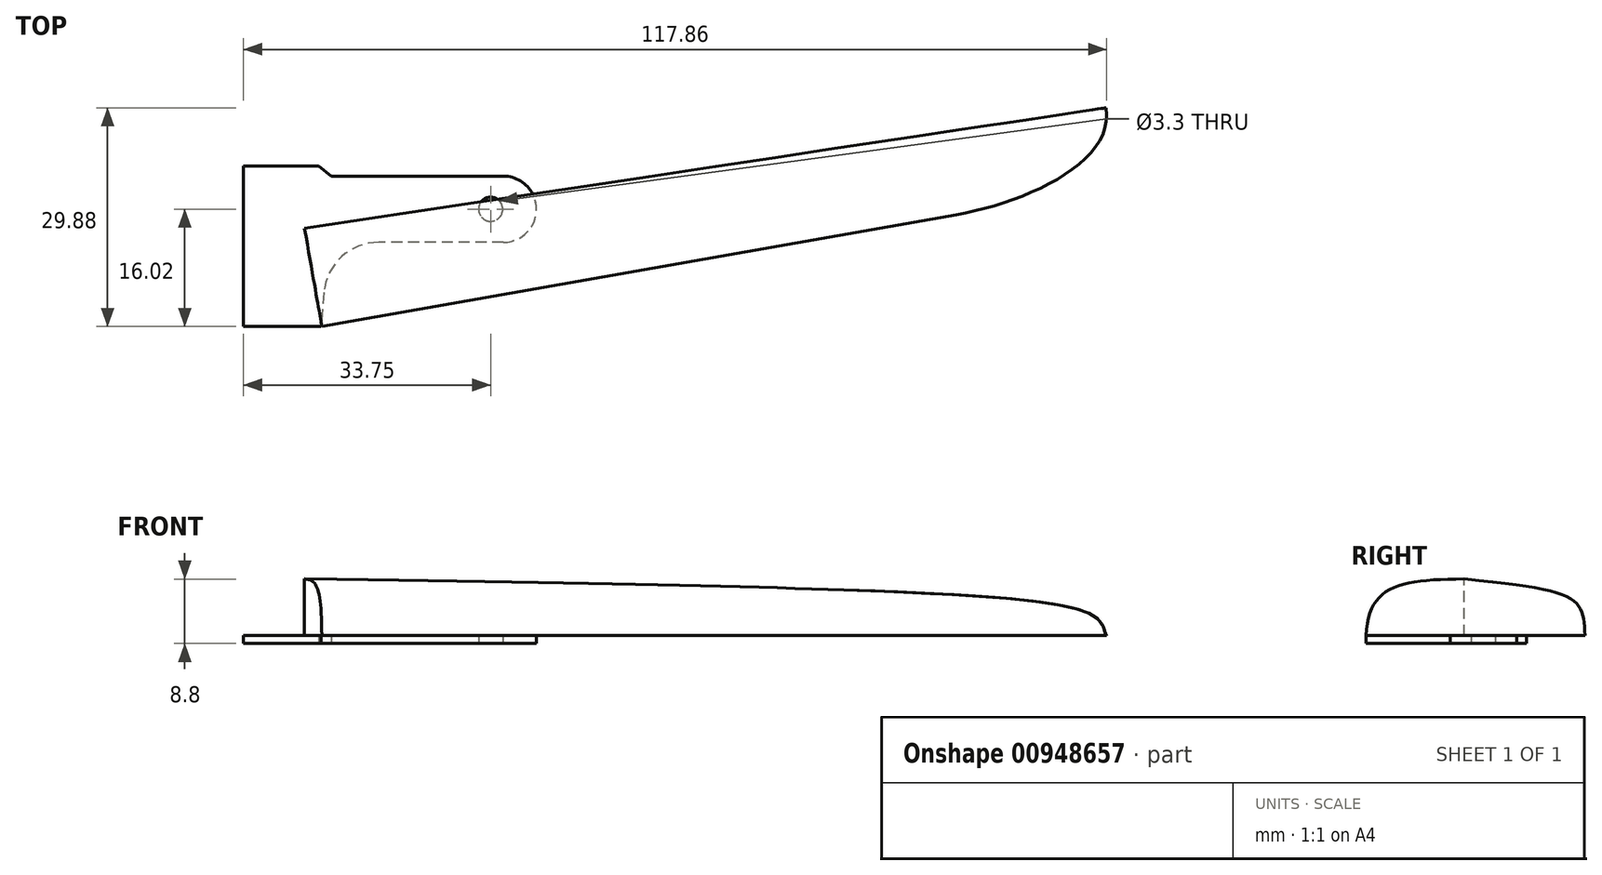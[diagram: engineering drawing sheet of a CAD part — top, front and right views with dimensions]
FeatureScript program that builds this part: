
annotation { "Feature Type Name" : "Feature", "Feature Type Description" : "" }
export const myFeature = defineFeature(function(context is Context, id is Id, definition is map)
    precondition{}
    {
        {
            var Q0;
            Q0=qCreatedBy(makeId("Top.planeOp"),FACE);
            var sketch = newSketch(context, id + "F0", { "sketchPlane" : qUnion([Q0]), "disableImprinting" : false});
            skCircle(sketch, "E0", {"center": v(0, 0) * mm, "radius": 1.65 * mm});
            skLineSegment(sketch, "E1", {"start": v(1.73, 4.52) * mm, "end": v(-21.75, 4.52) * mm});
            skArc(sketch, "E2", {"start": v(1.73, 4.52) * mm, "mid": v(6.25, 0) * mm, "end": v(1.73, -4.52) * mm});
            skLineSegment(sketch, "E3", {"start": v(1.73, -4.52) * mm, "end": v(-15.28, -4.52) * mm});
            skLineSegment(sketch, "E4", {"start": v(6.25, 0) * mm, "end": v(1.65, 0) * mm, "construction": true});
            skLineSegment(sketch, "E5", {"start": v(-21.75, 4.52) * mm, "end": v(-23.45, 5.9) * mm});
            skLineSegment(sketch, "E6", {"start": v(-23.45, 5.9) * mm, "end": v(-33.75, 5.9) * mm});
            skArc(sketch, "E7", {"start": v(-15.28, -4.52) * mm, "mid": v(-20.35, -6.5) * mm, "end": v(-22.75, -11.38) * mm});
            skLineSegment(sketch, "E8", {"start": v(-22.75, -11.38) * mm, "end": v(-23.15, -16.02) * mm});
            skLineSegment(sketch, "E9", {"start": v(-23.15, -16.02) * mm, "end": v(-33.75, -16.02) * mm});
            skLineSegment(sketch, "E10", {"start": v(-33.75, -16.02) * mm, "end": v(-33.75, 5.9) * mm});
            skSolve(sketch);
        }
        {
            var Q0;
            Q0 = qSketchRegion(id + "F0", true);
            extrude(context, id + "F1", {"entities" : qUnion([Q0]), "flatOperationType" : FlatOperationType.REMOVE, "thickness1" : 5 * mm, "thickness2" : 0 * mm, "thickness" : 5 * mm, "depth" : 1.06 * mm, "offsetDistance" : 25 * mm, "startOffsetBound" : StartOffsetType.BLIND, "startOffsetDistance" : 25 * mm, "symmetric" : true, "domain" : OperationDomain.MODEL});
        }
        {
            var Q0;
            Q0=makeQuery(id+"F1.opExtrude","CAP_FACE",FACE,{"disambiguationData":[OSD([sQuery(id+"F0.wireOp",EDGE,"E0"),sQuery(id+"F0.wireOp",EDGE,"E1"),sQuery(id+"F0.wireOp",EDGE,"E2"),sQuery(id+"F0.wireOp",EDGE,"E3"),sQuery(id+"F0.wireOp",EDGE,"E5"),sQuery(id+"F0.wireOp",EDGE,"E6"),sQuery(id+"F0.wireOp",EDGE,"E7"),sQuery(id+"F0.wireOp",EDGE,"E8"),sQuery(id+"F0.wireOp",EDGE,"E9"),sQuery(id+"F0.wireOp",EDGE,"E10")])],"isStart":false});
            var sketch = newSketch(context, id + "F2", { "sketchPlane" : qUnion([Q0])});
            skLineSegment(sketch, "E11.0", {"start": v(-21.75, 4.52) * mm, "end": v(-23.45, 5.9) * mm, "construction": true});
            skLineSegment(sketch, "E11.1", {"start": v(1.73, 4.52) * mm, "end": v(-21.75, 4.52) * mm, "construction": true});
            skArc(sketch, "E11.2", {"start": v(1.73, 4.52) * mm, "mid": v(6.25, 0) * mm, "end": v(1.73, -4.52) * mm, "construction": true});
            skLineSegment(sketch, "E11.3", {"start": v(1.73, -4.52) * mm, "end": v(-15.28, -4.52) * mm, "construction": true});
            skArc(sketch, "E11.4", {"start": v(-15.28, -4.52) * mm, "mid": v(-20.35, -6.5) * mm, "end": v(-22.75, -11.38) * mm, "construction": true});
            skLineSegment(sketch, "E11.5", {"start": v(-22.75, -11.38) * mm, "end": v(-23.15, -16.02) * mm, "construction": true});
            skLineSegment(sketch, "E11.6", {"start": v(-23.45, 5.9) * mm, "end": v(-33.75, 5.9) * mm, "construction": true});
            skLineSegment(sketch, "E11.7", {"start": v(-23.15, -16.02) * mm, "end": v(-33.75, -16.02) * mm, "construction": true});
            skLineSegment(sketch, "E12.0", {"start": v(-23.41, 6) * mm, "end": v(-27, 6) * mm});
            skLineSegment(sketch, "E12.1", {"start": v(-21.71, 4.62) * mm, "end": v(-23.41, 6) * mm});
            skLineSegment(sketch, "E12.2", {"start": v(1.73, 4.62) * mm, "end": v(-21.71, 4.62) * mm});
            skArc(sketch, "E12.3", {"start": v(1.73, 4.62) * mm, "mid": v(6.35, 0) * mm, "end": v(1.73, -4.62) * mm});
            skLineSegment(sketch, "E12.5", {"start": v(-22.65, -11.38) * mm, "end": v(-23.05, -16.02) * mm});
            skArc(sketch, "E12.6", {"start": v(-15.28, -4.62) * mm, "mid": v(-20.28, -6.57) * mm, "end": v(-22.65, -11.38) * mm});
            skLineSegment(sketch, "E12.7", {"start": v(1.73, -4.62) * mm, "end": v(-15.28, -4.62) * mm});
            skLineSegment(sketch, "E13", {"start": v(-27, 6) * mm, "end": v(-27, 10) * mm});
            skLineSegment(sketch, "E14", {"start": v(-27, 10) * mm, "end": v(81.33, 29.1) * mm, "construction": true});
            skLineSegment(sketch, "E15", {"start": v(81.33, 29.1) * mm, "end": v(85.9, 3.2) * mm, "construction": true});
            skLineSegment(sketch, "E16", {"start": v(85.9, 3.2) * mm, "end": v(-23.05, -16.02) * mm, "construction": true});
            skLineSegment(sketch, "E17", {"start": v(-23.05, -16.02) * mm, "end": v(-23.15, -16.02) * mm, "construction": true});
            skLineSegment(sketch, "E18", {"start": v(-10.66, -11.4) * mm, "end": v(-10.25, -13.76) * mm, "construction": true});
            skLineSegment(sketch, "E19", {"start": v(-23.05, -16.02) * mm, "end": v(-19.11, -15.33) * mm});
            skArc(sketch, "E20", {"start": v(-1.38, -12.2) * mm, "mid": v(-10.66, -11.4) * mm, "end": v(-19.11, -15.33) * mm});
            skPoint(sketch, "E20.second.point", {"position": v(-1.38, -12.2) * mm});
            skLineSegment(sketch, "E21.1.0.0", {"start": v(-1.38, -12.2) * mm, "end": v(2.56, -11.5) * mm});
            skArc(sketch, "E21.1.0.1", {"start": v(20.28, -8.38) * mm, "mid": v(11, -7.58) * mm, "end": v(2.56, -11.5) * mm});
            skLineSegment(sketch, "E21.2.0.0", {"start": v(20.28, -8.38) * mm, "end": v(24.22, -7.68) * mm});
            skArc(sketch, "E21.2.0.1", {"start": v(41.95, -4.56) * mm, "mid": v(32.67, -3.76) * mm, "end": v(24.22, -7.68) * mm});
            skLineSegment(sketch, "E21.3.0.0", {"start": v(41.95, -4.56) * mm, "end": v(45.89, -3.86) * mm});
            skArc(sketch, "E21.3.0.1", {"start": v(63.61, -0.74) * mm, "mid": v(54.33, 0.06) * mm, "end": v(45.89, -3.86) * mm});
            skLineSegment(sketch, "E21.direction1", {"start": v(-23.05, -16.02) * mm, "end": v(-1.38, -12.2) * mm, "construction": true});
            skPoint(sketch, "E22", {"position": v(27.16, 19.55) * mm});
            skPoint(sketch, "E23", {"position": v(84.02, 13.86) * mm});
            skFitSpline(sketch, "E24", {"points": [v(63.61, -0.74) * mm, v(84.02, 13.86) * mm], "startDerivative": vector(28.55, 5.03) * mm, "endDerivative": vector(-3.93, 22.27) * mm});
            skFitSpline(sketch, "E25", {"points": [v(84.02, 13.86) * mm, v(41.22, 22.03) * mm, v(-27, 10) * mm], "startDerivative": vector(-11.45, 64.92) * mm, "endDerivative": vector(-129.45, -32.73) * mm});
            skLineSegment(sketch, "E26", {"start": v(-23.05, -16.02) * mm, "end": v(-27.61, 9.85) * mm, "construction": true});
            skLineSegment(sketch, "E27", {"start": v(-27, 10) * mm, "end": v(-27.61, 9.85) * mm, "construction": true});
            skLineSegment(sketch, "E28", {"start": v(-19.11, -15.33) * mm, "end": v(63.61, -0.74) * mm});
            skSolve(sketch);
        }
        {
            var Q0;
            Q0=sQuery(id+"F2.wireOp",EDGE,"E16");
            var Q1;
            Q1=sQuery(id+"F2.wireOp",VERTEX,"E12.5.end");
            cPlane(context, id + "F3", {"entities" : qUnion([Q0, Q1]), "cplaneType" : CPlaneType.LINE_POINT, "offset" : 25 * mm, "width" : 150 * mm, "height" : 150 * mm});
        }
        {
            var Q0;
            Q0=qCreatedBy(id+"F3.planeOp",FACE);
            var sketch = newSketch(context, id + "F4", { "sketchPlane" : qUnion([Q0])});
            skLineSegment(sketch, "E29", {"start": v(11.77, 0.53) * mm, "end": v(-1.83, 0.53) * mm});
            skLineSegment(sketch, "E30", {"start": v(-1.83, 0.53) * mm, "end": v(-1.83, 8.27) * mm});
            skFitSpline(sketch, "E31", {"points": [v(11.77, 0.53) * mm, v(-1.83, 8.27) * mm], "startDerivative": vector(-0.83, 20.65) * mm, "endDerivative": vector(-26.9, 0.16) * mm});
            skSolve(sketch);
        }
        {
            var Q0;
            Q0=sQuery(id+"F4.wireOp",VERTEX,"E30.end");
            var Q1;
            Q1=sQuery(id+"F4.wireOp",VERTEX,"E29.end");
            var Q2;
            Q2=sQuery(id+"F2.wireOp",VERTEX,"E23");
            cPlane(context, id + "F5", {"entities" : qUnion([Q0, Q1, Q2]), "cplaneType" : CPlaneType.THREE_POINT, "offset" : 25 * mm, "width" : 150 * mm, "height" : 150 * mm});
        }
        {
            var Q0;
            Q0=qCreatedBy(id+"F5.planeOp",FACE);
            var sketch = newSketch(context, id + "F6", { "sketchPlane" : qUnion([Q0])});
            skLineSegment(sketch, "E32", {"start": v(25.52, 0.53) * mm, "end": v(-85.14, 0.53) * mm});
            skFitSpline(sketch, "E33", {"points": [v(25.52, 8.27) * mm, v(-85.14, 0.53) * mm], "startDerivative": vector(-326.42, -4.58) * mm, "endDerivative": vector(-3.65, -15.13) * mm});
            skSolve(sketch);
        }
        {
            var Q0;
            Q0=makeQuery(id+"F4.imprint","IMPRINT",FACE,{"disambiguationData":[TD([[makeQuery(id+"F4.imprint","IMPRINT",EDGE,{"derivedFrom":sQuery(id+"F4.wireOp",EDGE,"E29")}),-1.0]])]});
            var Q1;
            Q1=sQuery(id+"F2.wireOp",VERTEX,"E23");
            var Q2;
            Q2=sQuery(id+"F6.wireOp",EDGE,"E33");
            var Q3;
            Q3=sQuery(id+"F6.wireOp",EDGE,"E32");
            var Q4;
            Q4=sQuery(id+"F2.wireOp",EDGE,"E19");
            var Q5;
            Q5=sQuery(id+"F2.wireOp",EDGE,"E28");
            var Q6;
            Q6=sQuery(id+"F2.wireOp",EDGE,"E24");
            loft(context, id + "F7", {"sheetProfilesArray" : [{ "sheetProfileEntities" : qUnion([Q0]) }, { "sheetProfileEntities" : qUnion([Q1]) }], "addGuides" : true, "guidesArray" : [{ "guideEntities" : qUnion([Q2]), "guideDerivativeType" : LoftGuideDerivativeType.DEFAULT, "guideDerivativeMagnitude" : 1 }, { "guideEntities" : qUnion([Q3]), "guideDerivativeType" : LoftGuideDerivativeType.DEFAULT, "guideDerivativeMagnitude" : 1 }, { "guideEntities" : qUnion([Q4, Q5, Q6]), "guideDerivativeType" : LoftGuideDerivativeType.DEFAULT, "guideDerivativeMagnitude" : 1 }]});
        }
    });
